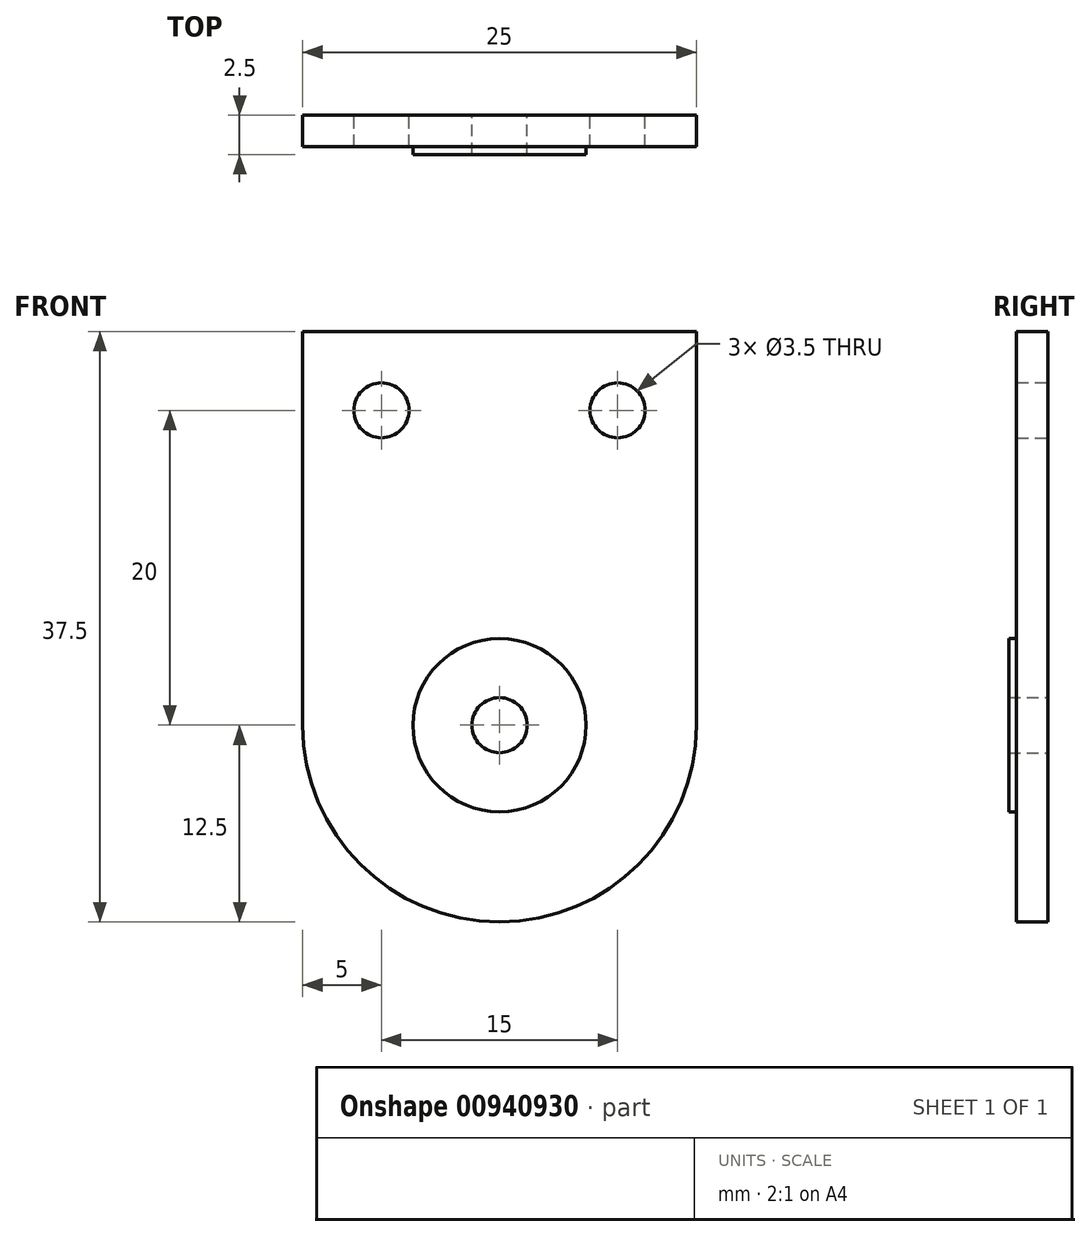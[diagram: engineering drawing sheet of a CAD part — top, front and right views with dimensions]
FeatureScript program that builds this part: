
annotation { "Feature Type Name" : "Feature", "Feature Type Description" : "" }
export const myFeature = defineFeature(function(context is Context, id is Id, definition is map)
    precondition{}
    {
        {
            var Q0;
            Q0=qCreatedBy(makeId("Front.planeOp"),FACE);
            var sketch = newSketch(context, id + "F0", { "sketchPlane" : qUnion([Q0])});
            skLineSegment(sketch, "E0.bottom", {"start": v(-12.5, 25) * mm, "end": v(12.5, 25) * mm});
            skLineSegment(sketch, "E0.top", {"start": v(-12.5, 0) * mm, "end": v(12.5, 0) * mm});
            skLineSegment(sketch, "E0.left", {"start": v(-12.5, 25) * mm, "end": v(-12.5, 0) * mm});
            skLineSegment(sketch, "E0.right", {"start": v(12.5, 25) * mm, "end": v(12.5, 0) * mm});
            skCircle(sketch, "E1", {"center": v(0, 0) * mm, "radius": 12.5 * mm});
            skCircle(sketch, "E2", {"center": v(0, 0) * mm, "radius": 1.75 * mm});
            skCircle(sketch, "E3", {"center": v(-7.5, 20) * mm, "radius": 1.75 * mm});
            skCircle(sketch, "E4", {"center": v(7.5, 20) * mm, "radius": 1.75 * mm});
            skSolve(sketch);
        }
        {
            var Q0;
            Q0=qSketchRegion(id+"F0",true);
            extrude(context, id + "F1", {"entities" : qUnion([Q0]), "depth" : 2 * mm, "offsetDistance" : 25 * mm});
        }
        {
            var Q0;
            Q0=makeQuery(id+"F1.opExtrude","CAP_FACE",FACE,{"disambiguationData":[OSD([sQuery(id+"F0.wireOp",EDGE,"E0.bottom"),sQuery(id+"F0.wireOp",EDGE,"E0.left"),sQuery(id+"F0.wireOp",EDGE,"E0.right"),sQuery(id+"F0.wireOp",EDGE,"E1"),sQuery(id+"F0.wireOp",EDGE,"E2"),sQuery(id+"F0.wireOp",EDGE,"E3"),sQuery(id+"F0.wireOp",EDGE,"E4")])],"isStart":false});
            var sketch = newSketch(context, id + "F2", { "sketchPlane" : qUnion([Q0])});
            skCircle(sketch, "E5", {"center": v(0, 0) * mm, "radius": 1.75 * mm});
            skCircle(sketch, "E6", {"center": v(0, 0) * mm, "radius": 5.5 * mm});
            skSolve(sketch);
        }
        {
            var Q0;
            Q0=qSketchRegion(id+"F2",true);
            extrude(context, id + "F3", {"entities" : qUnion([Q0]), "operationType" : NewBodyOperationType.ADD, "depth" : 0.5 * mm, "offsetDistance" : 25 * mm});
        }
    });
